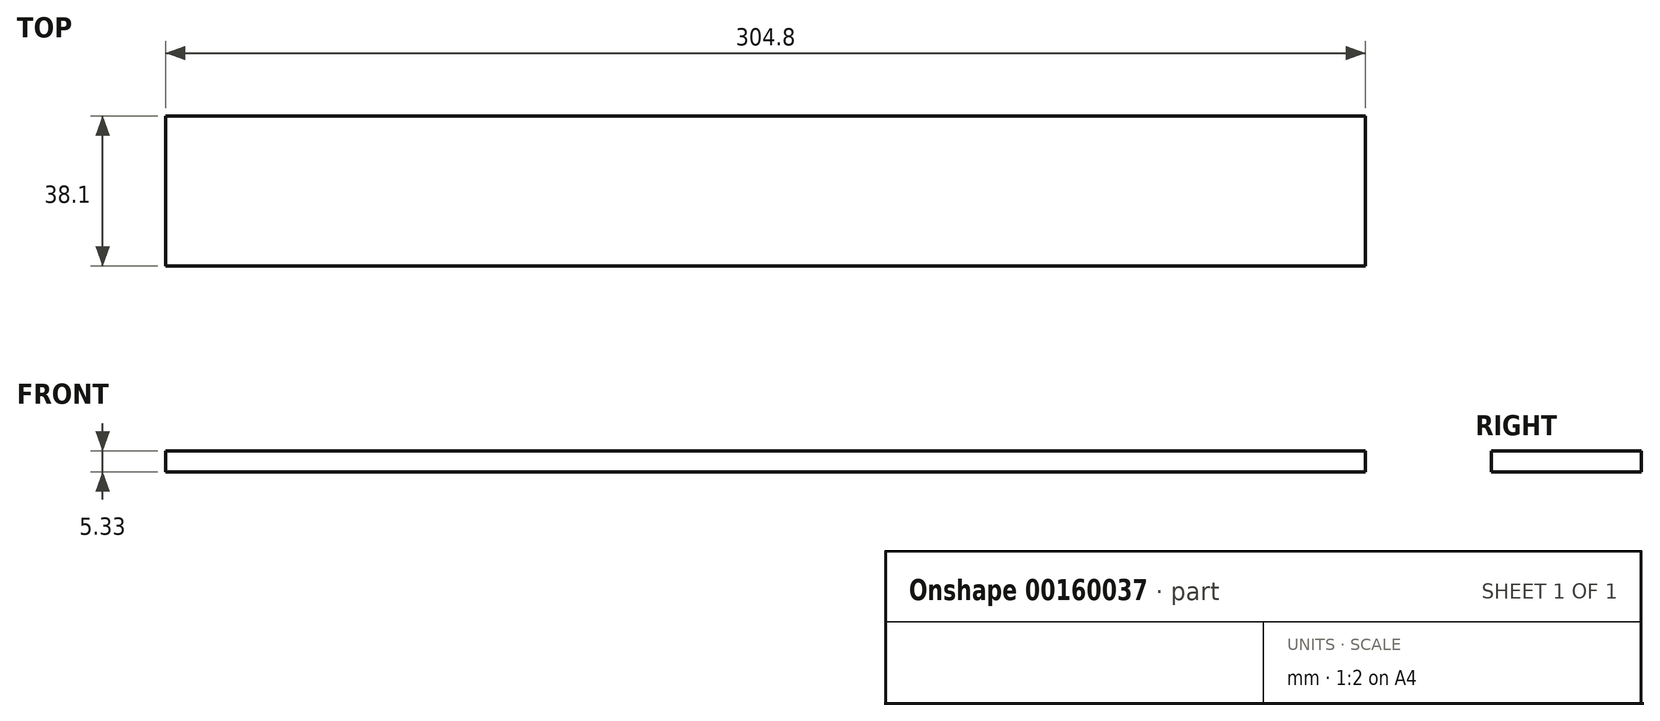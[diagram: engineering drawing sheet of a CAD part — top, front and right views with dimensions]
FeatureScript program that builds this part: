
annotation { "Feature Type Name" : "Feature", "Feature Type Description" : "" }
export const myFeature = defineFeature(function(context is Context, id is Id, definition is map)
    precondition{}
    {
        {
            var Q0;
            Q0=qCreatedBy(makeId("Top.planeOp"),FACE);
            var sketch = newSketch(context, id + "F0", { "sketchPlane" : qUnion([Q0])});
            skLineSegment(sketch, "E0.bottom", {"start": v(0, 0) * mm, "end": v(304.8, 0) * mm});
            skLineSegment(sketch, "E0.top", {"start": v(0, 38.1) * mm, "end": v(304.8, 38.1) * mm});
            skLineSegment(sketch, "E0.left", {"start": v(0, 0) * mm, "end": v(0, 38.1) * mm});
            skLineSegment(sketch, "E0.right", {"start": v(304.8, 0) * mm, "end": v(304.8, 38.1) * mm});
            skSolve(sketch);
        }
        {
            var Q0;
            Q0 = qSketchRegion(id + "F0", true);
            extrude(context, id + "F1", {"entities" : qUnion([Q0]), "depth" : 5.33 * mm});
        }
    });
